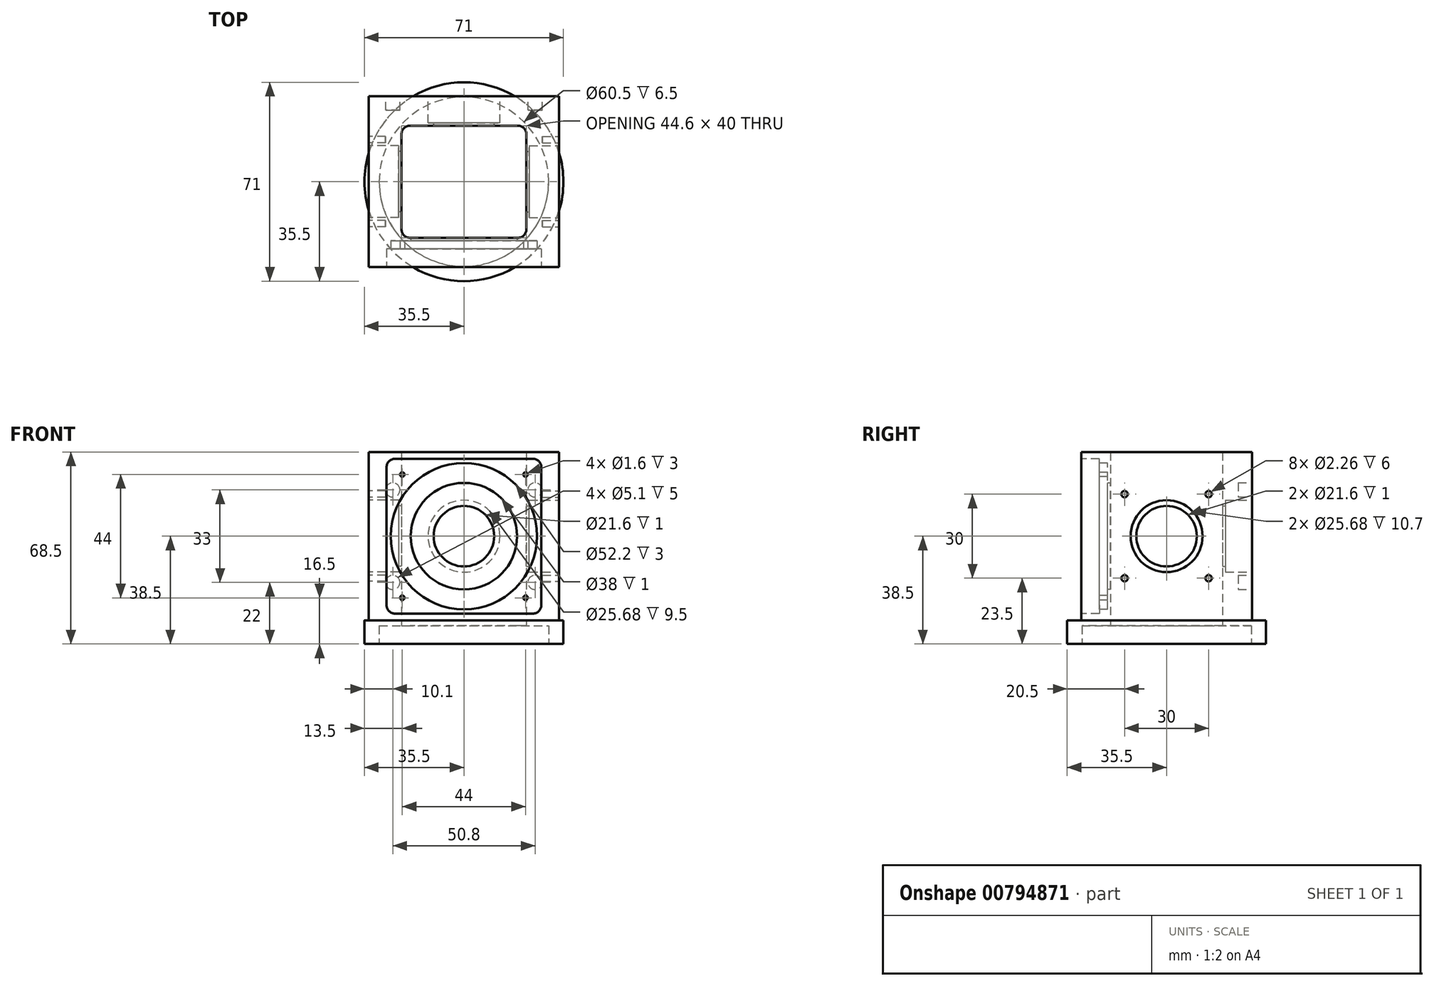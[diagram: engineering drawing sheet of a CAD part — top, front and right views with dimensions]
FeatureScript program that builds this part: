
annotation { "Feature Type Name" : "Feature", "Feature Type Description" : "" }
export const myFeature = defineFeature(function(context is Context, id is Id, definition is map)
    precondition{}
    {
        {
            var Q0;
            Q0=qCreatedBy(makeId("Top.planeOp"),FACE);
            var sketch = newSketch(context, id + "F0", { "sketchPlane" : qUnion([Q0])});
            skCircle(sketch, "E0", {"center": v(0, 0) * mm, "radius": 30.25 * mm});
            skSolve(sketch);
        }
        {
            var Q0;
            Q0=qCreatedBy(makeId("Top.planeOp"),FACE);
            var sketch = newSketch(context, id + "F1", { "sketchPlane" : qUnion([Q0])});
            skCircle(sketch, "E1", {"center": v(0, 0) * mm, "radius": 35.5 * mm});
            skSolve(sketch);
        }
        {
            var Q0;
            Q0=qSketchRegion(id+"F1",true);
            extrude(context, id + "F2", {"entities" : qUnion([Q0]), "depth" : 8.5 * mm, "offsetDistance" : 25 * mm});
        }
        {
            var Q0;
            Q0=qSketchRegion(id+"F0",true);
            extrude(context, id + "F3", {"entities" : qUnion([Q0]), "operationType" : NewBodyOperationType.REMOVE, "depth" : 8.5 * mm, "offsetDistance" : 25 * mm});
        }
        {
            var Q0;
            Q0=makeQuery(id+"F2.opExtrude","CAP_FACE",FACE,{"disambiguationData":[OSD([sQuery(id+"F1.wireOp",EDGE,"E1")])],"isStart":false});
            var sketch = newSketch(context, id + "F4", { "sketchPlane" : qUnion([Q0])});
            skLineSegment(sketch, "E2.bottom", {"start": v(19.3, -20) * mm, "end": v(-19.3, -20) * mm});
            skLineSegment(sketch, "E2.top", {"start": v(19.3, 20) * mm, "end": v(-19.3, 20) * mm});
            skLineSegment(sketch, "E2.left", {"start": v(22.3, -17) * mm, "end": v(22.3, 17) * mm});
            skLineSegment(sketch, "E2.right", {"start": v(-22.3, -17) * mm, "end": v(-22.3, 17) * mm});
            skPoint(sketch, "E2.middle", {"position": v(0, 0) * mm});
            skPoint(sketch, "E3.visualSharp", {"position": v(-22.3, 20) * mm});
            skArc(sketch, "E3.filletArc", {"start": v(-19.3, 20) * mm, "mid": v(-21.42, 19.12) * mm, "end": v(-22.3, 17) * mm});
            skPoint(sketch, "E4.visualSharp", {"position": v(22.3, 20) * mm});
            skArc(sketch, "E4.filletArc", {"start": v(22.3, 17) * mm, "mid": v(21.42, 19.12) * mm, "end": v(19.3, 20) * mm});
            skPoint(sketch, "E5.visualSharp", {"position": v(22.3, -20) * mm});
            skArc(sketch, "E5.filletArc", {"start": v(19.3, -20) * mm, "mid": v(21.42, -19.12) * mm, "end": v(22.3, -17) * mm});
            skPoint(sketch, "E6.visualSharp", {"position": v(-22.3, -20) * mm});
            skArc(sketch, "E6.filletArc", {"start": v(-22.3, -17) * mm, "mid": v(-21.42, -19.12) * mm, "end": v(-19.3, -20) * mm});
            skSolve(sketch);
        }
        {
            var Q0;
            Q0=makeQuery(id+"F4.imprint","IMPRINT",FACE,{"disambiguationData":[TD([[makeQuery(id+"F4.imprint","IMPRINT",EDGE,{"derivedFrom":makeQuery(id+"F2.opExtrude","CAP_EDGE",EDGE,{"disambiguationData":[OSD([sQuery(id+"F1.wireOp",EDGE,"E1")])],"isStart":false})}),1.0]])]});
            var sketch = newSketch(context, id + "F5", { "sketchPlane" : qUnion([Q0])});
            skLineSegment(sketch, "E7.bottom", {"start": v(-34, 0) * mm, "end": v(34, 0) * mm});
            skLineSegment(sketch, "E7.top", {"start": v(-34, 30.5) * mm, "end": v(34, 30.5) * mm});
            skLineSegment(sketch, "E7.left", {"start": v(-34, 0) * mm, "end": v(-34, 30.5) * mm});
            skLineSegment(sketch, "E7.right", {"start": v(34, 0) * mm, "end": v(34, 30.5) * mm});
            skLineSegment(sketch, "E8.top", {"start": v(-34, -30.5) * mm, "end": v(34, -30.5) * mm});
            skLineSegment(sketch, "E8.left", {"start": v(-34, 0) * mm, "end": v(-34, -30.5) * mm});
            skLineSegment(sketch, "E8.right", {"start": v(34, 0) * mm, "end": v(34, -30.5) * mm});
            skSolve(sketch);
        }
        {
            var Q0;
            Q0=qSketchRegion(id+"F5",true);
            extrude(context, id + "F6", {"entities" : qUnion([Q0]), "operationType" : NewBodyOperationType.ADD, "depth" : 60 * mm, "offsetDistance" : 25 * mm});
        }
        {
            var Q0;
            {var subQ0=makeQuery(id+"F3.boolean.opBoolean","COPY",FACE,{"derivedFrom":makeQuery(id+"F3.opExtrude","SWEPT_FACE",FACE,{"disambiguationData":[OSD([sQuery(id+"F0.wireOp",EDGE,"E0")])]})});var subQ1=sQuery(id+"F4.wireOp",EDGE,"E2.bottom");var subQ2=sQuery(id+"F5.wireOp",EDGE,"E8.left");var subQ3=sQuery(id+"F5.wireOp",EDGE,"E7.left");var subQ4=sQuery(id+"F5.wireOp",EDGE,"E7.top");var subQ5=sQuery(id+"F5.wireOp",EDGE,"E8.right");var subQ6=sQuery(id+"F5.wireOp",EDGE,"E7.right");Q0=makeQuery(id+"F9.boolean.opBoolean","SPLIT",FACE,{"disambiguationData":[TD([makeQuery(id+"F9.opExtrude","SWEPT_FACE",FACE,{"disambiguationData":[OSD([subQ1])]})])],"derivedFrom":makeQuery(id+"F6.boolean.opBoolean","SPLIT",FACE,{"disambiguationData":[TD([makeQuery(id+"F2.opExtrude","CAP_FACE",FACE,{"disambiguationData":[OSD([sQuery(id+"F1.wireOp",EDGE,"E1")])],"isStart":false}),subQ0,makeQuery(id+"F6.opExtrude","SWEPT_FACE",FACE,{"disambiguationData":[OSD([subQ4])]}),makeQuery(id+"F6.opExtrude","SWEPT_FACE",FACE,{"disambiguationData":[OSD([subQ3,subQ2])]}),makeQuery(id+"F6.opExtrude","SWEPT_FACE",FACE,{"disambiguationData":[OSD([subQ6,subQ5])]})])],"derivedFrom":makeQuery(id+"F6.opExtrude","CAP_FACE",FACE,{"disambiguationData":[OSD([subQ4,subQ3,subQ6,sQuery(id+"F5.wireOp",EDGE,"E8.top"),subQ2,subQ5])],"isStart":true})})});}
            var sketch = newSketch(context, id + "F7", { "sketchPlane" : qUnion([Q0])});
            skCircle(sketch, "E9", {"center": v(0, 0) * mm, "radius": 35.25 * mm});
            skSolve(sketch);
        }
        {
            var Q0;
            Q0=qSketchRegion(id+"F7",true);
            extrude(context, id + "F8", {"entities" : qUnion([Q0]), "operationType" : NewBodyOperationType.ADD, "depth" : 2 * mm, "offsetDistance" : 25 * mm});
        }
        {
            var Q0;
            Q0=qSketchRegion(id+"F4",true);
            extrude(context, id + "F9", {"entities" : qUnion([Q0]), "operationType" : NewBodyOperationType.REMOVE, "endBound" : BoundingType.SYMMETRIC, "depth" : 200 * mm, "offsetDistance" : 25 * mm});
        }
        {
            var Q0;
            Q0=makeQuery(id+"F6.opExtrude","SWEPT_FACE",FACE,{"disambiguationData":[OSD([sQuery(id+"F5.wireOp",EDGE,"E8.top")])]});
            var sketch = newSketch(context, id + "F10", { "sketchPlane" : qUnion([Q0])});
            skCircle(sketch, "E10", {"center": v(0, 38.5) * mm, "radius": 19 * mm});
            skSolve(sketch);
        }
        {
            var Q0;
            Q0=qSketchRegion(id+"F10",true);
            extrude(context, id + "F11", {"entities" : qUnion([Q0]), "operationType" : NewBodyOperationType.REMOVE, "oppositeDirection" : true, "depth" : 12 * mm, "offsetDistance" : 25 * mm});
        }
        {
            var Q0;
            Q0=makeQuery(id+"F6.opExtrude","SWEPT_FACE",FACE,{"disambiguationData":[OSD([sQuery(id+"F5.wireOp",EDGE,"E8.top")])]});
            var sketch = newSketch(context, id + "F12", { "sketchPlane" : qUnion([Q0])});
            skCircle(sketch, "E11", {"center": v(0, 38.5) * mm, "radius": 26.1 * mm});
            skSolve(sketch);
        }
        {
            var Q0;
            Q0=qSketchRegion(id+"F12",true);
            extrude(context, id + "F13", {"entities" : qUnion([Q0]), "operationType" : NewBodyOperationType.REMOVE, "oppositeDirection" : true, "depth" : 9.5 * mm, "offsetDistance" : 25 * mm});
        }
        {
            var Q0;
            Q0=makeQuery(id+"F6.opExtrude","SWEPT_FACE",FACE,{"disambiguationData":[OSD([sQuery(id+"F5.wireOp",EDGE,"E8.top")])]});
            var sketch = newSketch(context, id + "F14", { "sketchPlane" : qUnion([Q0])});
            skLineSegment(sketch, "E12.bottom", {"start": v(24.63, 10.88) * mm, "end": v(-24.62, 10.88) * mm});
            skLineSegment(sketch, "E12.top", {"start": v(24.63, 66.13) * mm, "end": v(-24.62, 66.13) * mm});
            skLineSegment(sketch, "E12.left", {"start": v(27.63, 13.88) * mm, "end": v(27.63, 63.13) * mm});
            skLineSegment(sketch, "E12.right", {"start": v(-27.62, 13.88) * mm, "end": v(-27.62, 63.13) * mm});
            skPoint(sketch, "E12.middle", {"position": v(0, 38.5) * mm});
            skPoint(sketch, "E13.visualSharp", {"position": v(-27.62, 66.13) * mm});
            skArc(sketch, "E13.filletArc", {"start": v(-24.62, 66.13) * mm, "mid": v(-26.75, 65.25) * mm, "end": v(-27.62, 63.13) * mm});
            skPoint(sketch, "E14.visualSharp", {"position": v(27.63, 66.13) * mm});
            skArc(sketch, "E14.filletArc", {"start": v(27.63, 63.13) * mm, "mid": v(26.75, 65.25) * mm, "end": v(24.63, 66.13) * mm});
            skPoint(sketch, "E15.visualSharp", {"position": v(27.63, 10.88) * mm});
            skArc(sketch, "E15.filletArc", {"start": v(24.63, 10.88) * mm, "mid": v(26.75, 11.75) * mm, "end": v(27.63, 13.88) * mm});
            skPoint(sketch, "E16.visualSharp", {"position": v(-27.62, 10.88) * mm});
            skArc(sketch, "E16.filletArc", {"start": v(-27.62, 13.88) * mm, "mid": v(-26.75, 11.75) * mm, "end": v(-24.62, 10.88) * mm});
            skSolve(sketch);
        }
        {
            var Q0;
            Q0=qSketchRegion(id+"F14",true);
            extrude(context, id + "F15", {"entities" : qUnion([Q0]), "operationType" : NewBodyOperationType.REMOVE, "oppositeDirection" : true, "depth" : 6.5 * mm, "offsetDistance" : 25 * mm});
        }
        {
            var Q0;
            Q0=makeQuery(id+"F6.opExtrude","SWEPT_FACE",FACE,{"disambiguationData":[OSD([sQuery(id+"F5.wireOp",EDGE,"E7.left"),sQuery(id+"F5.wireOp",EDGE,"E8.left")])]});
            var sketch = newSketch(context, id + "F16", { "sketchPlane" : qUnion([Q0])});
            skLineSegment(sketch, "E17", {"start": v(0, 0) * mm, "end": v(0, 38.5) * mm});
            skPoint(sketch, "E17.endSnap0", {"position": v(0, 8.5) * mm});
            skCircle(sketch, "E18", {"center": v(0, 38.5) * mm, "radius": 10.8 * mm});
            skSolve(sketch);
        }
        {
            var Q0;
            Q0=qSketchRegion(id+"F16",true);
            extrude(context, id + "F17", {"entities" : qUnion([Q0]), "operationType" : NewBodyOperationType.REMOVE, "oppositeDirection" : true, "depth" : 25 * mm, "offsetDistance" : 25 * mm});
        }
        {
            var Q0;
            Q0=makeQuery(id+"F6.opExtrude","SWEPT_FACE",FACE,{"disambiguationData":[OSD([sQuery(id+"F5.wireOp",EDGE,"E7.left"),sQuery(id+"F5.wireOp",EDGE,"E8.left")])]});
            var sketch = newSketch(context, id + "F18", { "sketchPlane" : qUnion([Q0])});
            skCircle(sketch, "E19", {"center": v(0, 38.5) * mm, "radius": 12.84 * mm});
            skSolve(sketch);
        }
        {
            var Q0;
            Q0=qSketchRegion(id+"F18",true);
            extrude(context, id + "F19", {"entities" : qUnion([Q0]), "operationType" : NewBodyOperationType.REMOVE, "oppositeDirection" : true, "depth" : 10.7 * mm, "offsetDistance" : 25 * mm});
        }
        {
            var Q0;
            Q0=makeQuery(id+"F6.opExtrude","SWEPT_FACE",FACE,{"disambiguationData":[OSD([sQuery(id+"F5.wireOp",EDGE,"E7.top")])]});
            var sketch = newSketch(context, id + "F20", { "sketchPlane" : qUnion([Q0])});
            skCircle(sketch, "E20", {"center": v(0, 38.5) * mm, "radius": 10.8 * mm});
            skSolve(sketch);
        }
        {
            var Q0;
            Q0=qSketchRegion(id+"F20",true);
            extrude(context, id + "F21", {"entities" : qUnion([Q0]), "operationType" : NewBodyOperationType.REMOVE, "oppositeDirection" : true, "depth" : 25 * mm, "offsetDistance" : 25 * mm});
        }
        {
            var Q0;
            Q0=makeQuery(id+"F6.opExtrude","SWEPT_FACE",FACE,{"disambiguationData":[OSD([sQuery(id+"F5.wireOp",EDGE,"E7.top")])]});
            var sketch = newSketch(context, id + "F22", { "sketchPlane" : qUnion([Q0])});
            skCircle(sketch, "E21", {"center": v(0, 38.5) * mm, "radius": 12.84 * mm});
            skSolve(sketch);
        }
        {
            var Q0;
            Q0=qSketchRegion(id+"F22",true);
            extrude(context, id + "F23", {"entities" : qUnion([Q0]), "operationType" : NewBodyOperationType.REMOVE, "oppositeDirection" : true, "depth" : 9.5 * mm, "offsetDistance" : 25 * mm});
        }
        {
            var Q0;
            Q0=makeQuery(id+"F15.boolean.opBoolean","COPY",FACE,{"derivedFrom":makeQuery(id+"F15.opExtrude","CAP_FACE",FACE,{"disambiguationData":[OSD([sQuery(id+"F14.wireOp",EDGE,"E12.bottom"),sQuery(id+"F14.wireOp",EDGE,"E12.top"),sQuery(id+"F14.wireOp",EDGE,"E12.left"),sQuery(id+"F14.wireOp",EDGE,"E12.right"),sQuery(id+"F14.wireOp",EDGE,"E13.filletArc"),sQuery(id+"F14.wireOp",EDGE,"E14.filletArc"),sQuery(id+"F14.wireOp",EDGE,"E15.filletArc"),sQuery(id+"F14.wireOp",EDGE,"E16.filletArc")])],"isStart":false})});
            var sketch = newSketch(context, id + "F24", { "sketchPlane" : qUnion([Q0])});
            skPoint(sketch, "E22.middle", {"position": v(0, 38.5) * mm});
            skCircle(sketch, "E23", {"center": v(-22, 60.5) * mm, "radius": 0.8 * mm});
            skCircle(sketch, "E24", {"center": v(22, 60.5) * mm, "radius": 0.8 * mm});
            skCircle(sketch, "E25", {"center": v(22, 16.5) * mm, "radius": 0.8 * mm});
            skCircle(sketch, "E26", {"center": v(-22, 16.5) * mm, "radius": 0.8 * mm});
            skSolve(sketch);
        }
        {
            var Q0;
            Q0=qSketchRegion(id+"F24",true);
            extrude(context, id + "F25", {"entities" : qUnion([Q0]), "operationType" : NewBodyOperationType.REMOVE, "oppositeDirection" : true, "depth" : 3 * mm, "offsetDistance" : 25 * mm});
        }
        {
            var Q0;
            Q0=makeQuery(id+"F6.opExtrude","SWEPT_FACE",FACE,{"disambiguationData":[OSD([sQuery(id+"F5.wireOp",EDGE,"E7.top")])]});
            var sketch = newSketch(context, id + "F26", { "sketchPlane" : qUnion([Q0])});
            skPoint(sketch, "E27.middle", {"position": v(0, 38.5) * mm});
            skCircle(sketch, "E28", {"center": v(-25.4, 55) * mm, "radius": 2.55 * mm});
            skCircle(sketch, "E29", {"center": v(25.4, 55) * mm, "radius": 2.55 * mm});
            skCircle(sketch, "E30", {"center": v(25.4, 22) * mm, "radius": 2.55 * mm});
            skCircle(sketch, "E31", {"center": v(-25.4, 22) * mm, "radius": 2.55 * mm});
            skSolve(sketch);
        }
        {
            var Q0;
            Q0=qSketchRegion(id+"F26",true);
            extrude(context, id + "F27", {"entities" : qUnion([Q0]), "operationType" : NewBodyOperationType.REMOVE, "oppositeDirection" : true, "depth" : 5 * mm, "offsetDistance" : 25 * mm});
        }
        {
            var Q0;
            Q0=makeQuery(id+"F6.opExtrude","SWEPT_FACE",FACE,{"disambiguationData":[OSD([sQuery(id+"F5.wireOp",EDGE,"E7.right"),sQuery(id+"F5.wireOp",EDGE,"E8.right")])]});
            var sketch = newSketch(context, id + "F28", { "sketchPlane" : qUnion([Q0])});
            skPoint(sketch, "E32.endSnap0", {"position": v(0, 8.5) * mm});
            skCircle(sketch, "E33", {"center": v(0, 38.5) * mm, "radius": 10.8 * mm});
            skSolve(sketch);
        }
        {
            var Q0;
            Q0=qSketchRegion(id+"F28",true);
            extrude(context, id + "F29", {"entities" : qUnion([Q0]), "operationType" : NewBodyOperationType.REMOVE, "oppositeDirection" : true, "depth" : 25 * mm, "offsetDistance" : 25 * mm});
        }
        {
            var Q0;
            Q0=makeQuery(id+"F6.opExtrude","SWEPT_FACE",FACE,{"disambiguationData":[OSD([sQuery(id+"F5.wireOp",EDGE,"E7.right"),sQuery(id+"F5.wireOp",EDGE,"E8.right")])]});
            var sketch = newSketch(context, id + "F30", { "sketchPlane" : qUnion([Q0])});
            skCircle(sketch, "E34", {"center": v(0, 38.5) * mm, "radius": 12.84 * mm});
            skSolve(sketch);
        }
        {
            var Q0;
            Q0=qSketchRegion(id+"F30",true);
            extrude(context, id + "F31", {"entities" : qUnion([Q0]), "operationType" : NewBodyOperationType.REMOVE, "oppositeDirection" : true, "depth" : 10.7 * mm, "offsetDistance" : 25 * mm});
        }
        {
            var Q0;
            Q0=makeQuery(id+"F6.opExtrude","SWEPT_FACE",FACE,{"disambiguationData":[OSD([sQuery(id+"F5.wireOp",EDGE,"E7.right"),sQuery(id+"F5.wireOp",EDGE,"E8.right")])]});
            var sketch = newSketch(context, id + "F32", { "sketchPlane" : qUnion([Q0])});
            skPoint(sketch, "E35.middle", {"position": v(0, 38.5) * mm});
            skCircle(sketch, "E36", {"center": v(-15, 53.5) * mm, "radius": 1.13 * mm});
            skCircle(sketch, "E37", {"center": v(15, 53.5) * mm, "radius": 1.13 * mm});
            skCircle(sketch, "E38", {"center": v(15, 23.5) * mm, "radius": 1.13 * mm});
            skCircle(sketch, "E39", {"center": v(-15, 23.5) * mm, "radius": 1.13 * mm});
            skSolve(sketch);
        }
        {
            var Q0;
            Q0=qSketchRegion(id+"F32",true);
            extrude(context, id + "F33", {"entities" : qUnion([Q0]), "operationType" : NewBodyOperationType.REMOVE, "oppositeDirection" : true, "depth" : 6 * mm, "offsetDistance" : 25 * mm});
        }
        {
            var Q0;
            Q0=makeQuery(id+"F6.opExtrude","SWEPT_FACE",FACE,{"disambiguationData":[OSD([sQuery(id+"F5.wireOp",EDGE,"E7.left"),sQuery(id+"F5.wireOp",EDGE,"E8.left")])]});
            var sketch = newSketch(context, id + "F34", { "sketchPlane" : qUnion([Q0])});
            skPoint(sketch, "E40.middle", {"position": v(0, 38.5) * mm});
            skCircle(sketch, "E41", {"center": v(-15, 23.5) * mm, "radius": 1.13 * mm});
            skCircle(sketch, "E42", {"center": v(15, 23.5) * mm, "radius": 1.13 * mm});
            skCircle(sketch, "E43", {"center": v(15, 53.5) * mm, "radius": 1.13 * mm});
            skCircle(sketch, "E44", {"center": v(-15, 53.5) * mm, "radius": 1.13 * mm});
            skSolve(sketch);
        }
        {
            var Q0;
            Q0=qSketchRegion(id+"F34",true);
            extrude(context, id + "F35", {"entities" : qUnion([Q0]), "operationType" : NewBodyOperationType.REMOVE, "oppositeDirection" : true, "depth" : 6 * mm, "offsetDistance" : 25 * mm});
        }
    });
